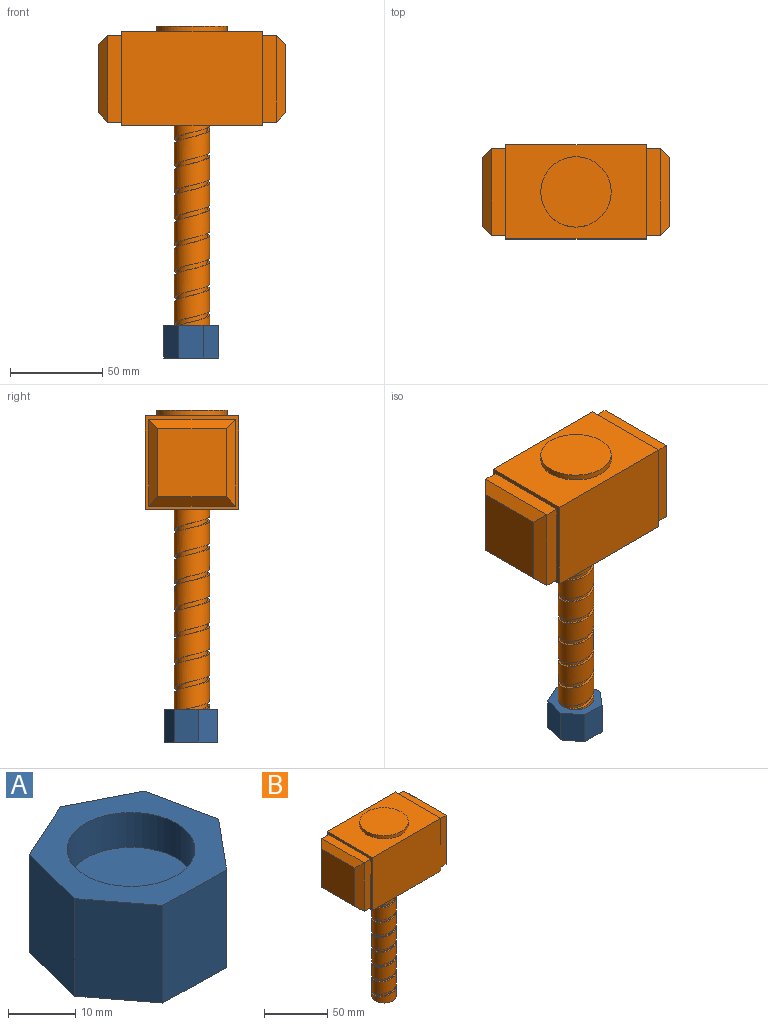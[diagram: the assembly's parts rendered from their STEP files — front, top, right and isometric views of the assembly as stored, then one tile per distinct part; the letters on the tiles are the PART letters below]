
ASSEMBLY  parts=2 mates=1
PART A: 75 faces, bbox 29.6x29x17.8 mm
  f0: plane 29.62x29.02mm, normal (0,0,-1), area 558.9mm2, adj f1,f2,f3,f4,f5,f6,f7,f11
  f1: plane 17.78x11.76mm, normal (0.45,0.89,0), area 234.4mm2, adj f0,f2,f7,f8
  f2: plane 17.78x12mm, normal (-0.41,0.91,0), area 234.4mm2, adj f0,f1,f3,f8
  f3: plane 17.78x12.79mm, normal (-0.97,0.24,0), area 234.4mm2, adj f0,f2,f4,f8
  f4: plane 17.78x10.48mm, normal (-0.79,-0.61,0), area 234.4mm2, adj f0,f3,f5,f8
  f5: plane 17.78x13.18mm, normal (-0.02,-1,0), area 234.4mm2, adj f0,f4,f6,f8
  f6: plane 17.78x10.13mm, normal (0.77,-0.64,0), area 234.4mm2, adj f0,f5,f7,f8
  f7: plane 17.78x12.91mm, normal (0.98,0.2,0), area 234.4mm2, adj f0,f1,f6,f8
  f8: plane 29.62x29.02mm, normal (0,0,1), area 346.8mm2, adj f1,f2,f3,f4,f5,f6,f7,f9
  f9: cylinder r=9.53mm len=19.05mm, axis (0,0,1), area 380mm2, adj f8,f10
  f10: plane 19.05x19.05mm, normal (0,0,1), area 285mm2, adj f9
  f11: extruded ~0.66x0.38mm, area 0.3mm2, adj f0,f12,f18,f19
  f12: extruded ~0.66x0.38mm, area 0.3mm2, adj f0,f11,f13,f19
  f13: extruded ~0.68x0.38mm, area 0.3mm2, adj f0,f12,f14,f19
  f14: extruded ~0.67x0.38mm, area 0.3mm2, adj f0,f13,f15,f19
  f15: extruded ~0.65x0.38mm, area 0.3mm2, adj f0,f14,f16,f19
  f16: extruded ~0.66x0.38mm, area 0.3mm2, adj f0,f15,f17,f19
  f17: extruded ~0.67x0.38mm, area 0.3mm2, adj f0,f16,f18,f19
  f18: extruded ~0.69x0.38mm, area 0.3mm2, adj f0,f11,f17,f19
  f19: plane 1.83x1.78mm, normal (0,0,-1), area 2.7mm2, adj f11,f12,f13,f14,f15,f16,f17,f18
  f20: plane 1.99x0.38mm, normal (-1,0,0), area 0.8mm2, adj f21,f44,f45,f74
  f21: plane 1x0.38mm, normal (0,-1,0), area 0.4mm2, adj f20,f22,f45,f74
  f22: extruded ~1.36x0.95mm, area 0.7mm2, adj f21,f23,f45,f74
  f23: extruded ~0.79x0.38mm, area 0.3mm2, adj f22,f24,f45,f74
  f24: extruded ~0.99x0.38mm, area 0.4mm2, adj f23,f44,f45,f74
  f25: plane 0.94x0.38mm, normal (0,1,0), area 0.4mm2, adj f26,f42,f45,f46
  f26: plane 1.7x0.38mm, normal (-1,0,0), area 0.6mm2, adj f25,f27,f45,f46
  f27: plane 0.85x0.38mm, normal (0,-1,0), area 0.3mm2, adj f26,f28,f45,f46
  f28: extruded ~1.02x0.38mm, area 0.4mm2, adj f27,f29,f45,f46
  f29: extruded ~0.63x0.38mm, area 0.3mm2, adj f28,f30,f45,f46
  f30: extruded ~0.67x0.38mm, area 0.3mm2, adj f29,f42,f45,f46
  f31: plane 2.38x0.38mm, normal (0,1,0), area 0.9mm2, adj f0,f32,f43,f45
  f32: plane 7.65x0.38mm, normal (1,0,0), area 2.9mm2, adj f0,f31,f33,f45
  f33: plane 2.86x0.38mm, normal (0,-1,0), area 1.1mm2, adj f0,f32,f34,f45
  f34: extruded ~2.05x0.59mm, area 0.8mm2, adj f0,f33,f35,f45
  f35: extruded ~1.63x0.76mm, area 0.7mm2, adj f0,f34,f36,f45
  f36: extruded ~1.18x0.38mm, area 0.5mm2, adj f0,f35,f37,f45
  f37: extruded ~1.05x0.61mm, area 0.5mm2, adj f0,f36,f38,f45
  f38: plane 0.38x0.05mm, normal (-1,0,0), area 0mm2, adj f0,f37,f39,f45
  f39: extruded ~0.86x0.53mm, area 0.4mm2, adj f0,f38,f40,f45
  f40: extruded ~1.13x0.38mm, area 0.5mm2, adj f0,f39,f41,f45
  f41: extruded ~1.47x0.73mm, area 0.7mm2, adj f0,f40,f43,f45
  f42: extruded ~0.95x0.38mm, area 0.4mm2, adj f25,f30,f45,f46
  f43: extruded ~2.36x0.46mm, area 0.9mm2, adj f0,f31,f41,f45
  f44: plane 1.06x0.38mm, normal (0,1,0), area 0.4mm2, adj f20,f24,f45,f74
  f45: plane 7.65x5.67mm, normal (0,0,-1), area 31.9mm2, adj f20,f21,f22,f23,f24,f25,f26,f27
  f46: plane 2.19x1.7mm, normal (0,0,-1), area 3.4mm2, adj f25,f26,f27,f28,f29,f30,f42
  f47: extruded ~1.89x0.77mm, area 0.8mm2, adj f0,f48,f62,f63
  f48: extruded ~1.79x0.72mm, area 0.8mm2, adj f0,f47,f49,f63
  f49: extruded ~2.12x0.6mm, area 0.9mm2, adj f0,f48,f50,f63
  f50: plane 2.44x0.38mm, normal (0,1,0), area 0.9mm2, adj f0,f49,f51,f63
  f51: plane 7.65x0.38mm, normal (1,0,0), area 2.9mm2, adj f0,f50,f52,f63
  f52: plane 1.62x0.38mm, normal (0,-1,0), area 0.6mm2, adj f0,f51,f53,f63
  f53: plane 2.72x0.38mm, normal (-1,0,0), area 1mm2, adj f0,f52,f54,f63
  f54: plane 0.69x0.38mm, normal (0,-1,0), area 0.3mm2, adj f0,f53,f62,f63
  f55: plane 0.53x0.38mm, normal (0,1,0), area 0.2mm2, adj f56,f61,f63,f64
  f56: plane 2.27x0.38mm, normal (-1,0,0), area 0.9mm2, adj f55,f57,f63,f64
  f57: plane 0.74x0.38mm, normal (0,-1,0), area 0.3mm2, adj f56,f58,f63,f64
  f58: extruded ~0.98x0.38mm, area 0.4mm2, adj f57,f59,f63,f64
  f59: extruded ~0.84x0.38mm, area 0.4mm2, adj f58,f60,f63,f64
  f60: extruded ~0.86x0.38mm, area 0.4mm2, adj f59,f61,f63,f64
  f61: extruded ~1.12x0.38mm, area 0.4mm2, adj f55,f60,f63,f64
  f62: extruded ~2.19x0.65mm, area 0.9mm2, adj f0,f47,f54,f63
  f63: plane 7.65x5.28mm, normal (0,0,-1), area 23.9mm2, adj f47,f48,f49,f50,f51,f52,f53,f54
  f64: plane 2.27x2.02mm, normal (0,0,-1), area 4.1mm2, adj f55,f56,f57,f58,f59,f60,f61
  f65: extruded ~0.66x0.38mm, area 0.3mm2, adj f0,f66,f72,f73
  f66: extruded ~0.66x0.38mm, area 0.3mm2, adj f0,f65,f67,f73
  f67: extruded ~0.68x0.38mm, area 0.3mm2, adj f0,f66,f68,f73
  f68: extruded ~0.67x0.38mm, area 0.3mm2, adj f0,f67,f69,f73
  f69: extruded ~0.65x0.38mm, area 0.3mm2, adj f0,f68,f70,f73
  f70: extruded ~0.66x0.38mm, area 0.3mm2, adj f0,f69,f71,f73
  f71: extruded ~0.67x0.38mm, area 0.3mm2, adj f0,f70,f72,f73
  f72: extruded ~0.69x0.38mm, area 0.3mm2, adj f0,f65,f71,f73
  f73: plane 1.83x1.78mm, normal (0,0,-1), area 2.7mm2, adj f65,f66,f67,f68,f69,f70,f71,f72
  f74: plane 2.36x1.99mm, normal (0,0,-1), area 4.3mm2, adj f20,f21,f22,f23,f24,f44
PART B: 96 faces, bbox 101.6x50.8x169 mm
  f0: plane 19.05x19.05mm, normal (0,0,-1), area 266.4mm2, adj f27,f28,f29,f30,f31,f32,f33,f34
  f1: plane 50.8x50.8mm, normal (-1,0,0), area 372.6mm2, adj f3,f4,f5,f6,f14,f15,f16,f17
  f2: plane 50.8x50.8mm, normal (1,0,0), area 372.6mm2, adj f3,f4,f5,f6,f9,f10,f11,f12
  f3: plane 76.2x50.8mm, normal (0,-1,0), area 3871mm2, adj f1,f2,f5,f6
  f4: plane 76.2x50.8mm, normal (0,1,0), area 3871mm2, adj f1,f2,f5,f6
  f5: plane 76.2x50.8mm, normal (0,0,1), area 2730.9mm2, adj f1,f2,f3,f4,f7
  f6: plane 76.2x50.8mm, normal (0,0,-1), area 3585.9mm2, adj f1,f2,f3,f4,f27
  f7: cylinder r=19.05mm len=38.1mm, axis (0,0,-1), area 380mm2, adj f5,f8
  f8: plane 38.1x38.1mm, normal (0,0,1), area 1140.1mm2, adj f7
  f9: plane 46.99x7.62mm, normal (0,0,-1), area 358.1mm2, adj f2,f10,f12,f24
  f10: plane 46.99x7.62mm, normal (0,1,0), area 358.1mm2, adj f2,f9,f11,f26
  f11: plane 46.99x7.62mm, normal (0,0,1), area 358.1mm2, adj f2,f10,f12,f25
  f12: plane 46.99x7.62mm, normal (0,-1,0), area 358.1mm2, adj f2,f9,f11,f23
  f13: plane 36.83x36.83mm, normal (1,0,0), area 1356.4mm2, adj f23,f24,f25,f26
  f14: plane 46.99x7.62mm, normal (0,0,1), area 358.1mm2, adj f1,f15,f17,f19
  f15: plane 46.99x7.62mm, normal (0,1,0), area 358.1mm2, adj f1,f14,f16,f21
  f16: plane 46.99x7.62mm, normal (0,0,-1), area 358.1mm2, adj f1,f15,f17,f22
  f17: plane 46.99x7.62mm, normal (0,-1,0), area 358.1mm2, adj f1,f14,f16,f20
  f18: plane 36.83x36.83mm, normal (-1,0,0), area 1356.4mm2, adj f19,f20,f21,f22
  f19: plane 46.99x5.08mm, normal (-0.71,0,0.71), area 301.1mm2, adj f14,f18,f20,f21
  f20: plane 46.99x5.08mm, normal (-0.71,-0.71,0), area 301.1mm2, adj f17,f18,f19,f22
  f21: plane 46.99x5.08mm, normal (-0.71,0.71,0), area 301.1mm2, adj f15,f18,f19,f22
  f22: plane 46.99x5.08mm, normal (-0.71,0,-0.71), area 301.1mm2, adj f16,f18,f20,f21
  f23: plane 46.99x5.08mm, normal (0.71,-0.71,0), area 301.1mm2, adj f12,f13,f24,f25
  f24: plane 46.99x5.08mm, normal (0.71,0,-0.71), area 301.1mm2, adj f9,f13,f23,f26
  f25: plane 46.99x5.08mm, normal (0.71,0,0.71), area 301.1mm2, adj f11,f13,f23,f26
  f26: plane 46.99x5.08mm, normal (0.71,0.71,0), area 301.1mm2, adj f10,f13,f24,f25
  f27: cylinder r=9.53mm len=114.3mm, axis (0,0,1), area 5601.7mm2, adj f0,f6,f92,f93,f95
  f28: extruded ~15.88x0.19mm, area 3.3mm2, adj f0,f29,f35,f36
  f29: extruded ~15.88x0.19mm, area 3.3mm2, adj f0,f28,f30,f36
  f30: extruded ~15.88x0.2mm, area 3.4mm2, adj f0,f29,f31,f36
  f31: extruded ~15.88x0.19mm, area 3.3mm2, adj f0,f30,f32,f36
  f32: extruded ~15.88x0.19mm, area 3.3mm2, adj f0,f31,f33,f36
  f33: extruded ~15.88x0.19mm, area 3.3mm2, adj f0,f32,f34,f36
  f34: extruded ~15.88x0.19mm, area 3.3mm2, adj f0,f33,f35,f36
  f35: extruded ~15.88x0.2mm, area 3.4mm2, adj f0,f28,f34,f36
  f36: plane 0.53x0.51mm, normal (0,0,-1), area 0.2mm2, adj f28,f29,f30,f31,f32,f33,f34,f35
  f37: plane 15.88x0.57mm, normal (-1,0,0), area 9.1mm2, adj f38,f61,f62,f91
  f38: plane 15.88x0.29mm, normal (0,-1,0), area 4.6mm2, adj f37,f39,f62,f91
  f39: extruded ~15.88x0.39mm, area 8.6mm2, adj f38,f40,f62,f91
  f40: extruded ~15.88x0.23mm, area 4mm2, adj f39,f41,f62,f91
  f41: extruded ~15.88x0.28mm, area 4.7mm2, adj f40,f61,f62,f91
  f42: plane 15.88x0.27mm, normal (0,1,0), area 4.3mm2, adj f43,f59,f62,f63
  f43: plane 15.88x0.49mm, normal (-1,0,0), area 7.8mm2, adj f42,f44,f62,f63
  f44: plane 15.88x0.25mm, normal (0,-1,0), area 3.9mm2, adj f43,f45,f62,f63
  f45: extruded ~15.88x0.29mm, area 4.8mm2, adj f44,f46,f62,f63
  f46: extruded ~15.88x0.18mm, area 3.4mm2, adj f45,f47,f62,f63
  f47: extruded ~15.88x0.19mm, area 3.5mm2, adj f46,f59,f62,f63
  f48: plane 15.88x0.68mm, normal (0,1,0), area 10.9mm2, adj f0,f49,f60,f62
  f49: plane 15.88x2.2mm, normal (1,0,0), area 34.9mm2, adj f0,f48,f50,f62
  f50: plane 15.88x0.82mm, normal (0,-1,0), area 13.1mm2, adj f0,f49,f51,f62
  f51: extruded ~15.88x0.59mm, area 9.9mm2, adj f0,f50,f52,f62
  f52: extruded ~15.88x0.47mm, area 8.5mm2, adj f0,f51,f53,f62
  f53: extruded ~15.88x0.34mm, area 5.7mm2, adj f0,f52,f54,f62
  f54: extruded ~15.88x0.3mm, area 5.7mm2, adj f0,f53,f55,f62
  f55: plane 15.88x0.02mm, normal (-1,0,0), area 0.2mm2, adj f0,f54,f56,f62
  f56: extruded ~15.88x0.25mm, area 4.7mm2, adj f0,f55,f57,f62
  f57: extruded ~15.88x0.32mm, area 5.4mm2, adj f0,f56,f58,f62
  f58: extruded ~15.88x0.42mm, area 7.9mm2, adj f0,f57,f60,f62
  f59: extruded ~15.88x0.27mm, area 4.5mm2, adj f42,f47,f62,f63
  f60: extruded ~15.88x0.68mm, area 11.1mm2, adj f0,f48,f58,f62
  f61: plane 15.88x0.3mm, normal (0,1,0), area 4.8mm2, adj f37,f41,f62,f91
  f62: plane 2.2x1.63mm, normal (0,0,-1), area 2.6mm2, adj f37,f38,f39,f40,f41,f42,f43,f44
  f63: plane 0.63x0.49mm, normal (0,0,-1), area 0.3mm2, adj f42,f43,f44,f45,f46,f47,f59
  f64: extruded ~15.88x0.54mm, area 9.6mm2, adj f0,f65,f79,f80
  f65: extruded ~15.88x0.51mm, area 9.1mm2, adj f0,f64,f66,f80
  f66: extruded ~15.88x0.61mm, area 10.2mm2, adj f0,f65,f67,f80
  f67: plane 15.88x0.7mm, normal (0,1,0), area 11.1mm2, adj f0,f66,f68,f80
  f68: plane 15.88x2.2mm, normal (1,0,0), area 34.9mm2, adj f0,f67,f69,f80
  f69: plane 15.88x0.47mm, normal (0,-1,0), area 7.4mm2, adj f0,f68,f70,f80
  f70: plane 15.88x0.78mm, normal (-1,0,0), area 12.4mm2, adj f0,f69,f71,f80
  f71: plane 15.88x0.2mm, normal (0,-1,0), area 3.2mm2, adj f0,f70,f79,f80
  f72: plane 15.88x0.15mm, normal (0,1,0), area 2.4mm2, adj f73,f78,f80,f81
  f73: plane 15.88x0.65mm, normal (-1,0,0), area 10.4mm2, adj f72,f74,f80,f81
  f74: plane 15.88x0.21mm, normal (0,-1,0), area 3.4mm2, adj f73,f75,f80,f81
  f75: extruded ~15.88x0.28mm, area 4.7mm2, adj f74,f76,f80,f81
  f76: extruded ~15.88x0.24mm, area 4.2mm2, adj f75,f77,f80,f81
  f77: extruded ~15.88x0.25mm, area 4.4mm2, adj f76,f78,f80,f81
  f78: extruded ~15.88x0.32mm, area 5.4mm2, adj f72,f77,f80,f81
  f79: extruded ~15.88x0.63mm, area 10.7mm2, adj f0,f64,f71,f80
  f80: plane 2.2x1.52mm, normal (0,0,-1), area 2mm2, adj f64,f65,f66,f67,f68,f69,f70,f71
  f81: plane 0.65x0.58mm, normal (0,0,-1), area 0.3mm2, adj f72,f73,f74,f75,f76,f77,f78
  f82: extruded ~15.88x0.19mm, area 3.3mm2, adj f0,f83,f89,f90
  f83: extruded ~15.88x0.19mm, area 3.3mm2, adj f0,f82,f84,f90
  f84: extruded ~15.88x0.2mm, area 3.4mm2, adj f0,f83,f85,f90
  f85: extruded ~15.88x0.19mm, area 3.3mm2, adj f0,f84,f86,f90
  f86: extruded ~15.88x0.19mm, area 3.3mm2, adj f0,f85,f87,f90
  f87: extruded ~15.88x0.19mm, area 3.3mm2, adj f0,f86,f88,f90
  f88: extruded ~15.88x0.19mm, area 3.3mm2, adj f0,f87,f89,f90
  f89: extruded ~15.88x0.2mm, area 3.4mm2, adj f0,f82,f88,f90
  f90: plane 0.53x0.51mm, normal (0,0,-1), area 0.2mm2, adj f82,f83,f84,f85,f86,f87,f88,f89
  f91: plane 0.68x0.57mm, normal (0,0,-1), area 0.4mm2, adj f37,f38,f39,f40,f41,f61
  f92: plane 2.54x1.27mm, normal (0,-1,0), area 3.2mm2, adj f27,f93,f94,f95
  f93: bspline ~114.3x19.05mm, area 586.4mm2, adj f0,f27,f92,f94
  f94: cylinder r=8.26mm len=114.3mm, axis (0,0,-1), area 1208.7mm2, adj f0,f92,f93,f95
  f95: bspline ~112.51x19.05mm, area 572.7mm2, adj f0,f27,f92,f94
PLACE A t=(-0.72,0.29,-6.75)mm fixed
PLACE B t=(-38.49,-24.9,118.98)mm
MATE fastened B.f0 <-> A.f9  axis (0,0,-1) through (-0.72,0.29,4.68)mm
